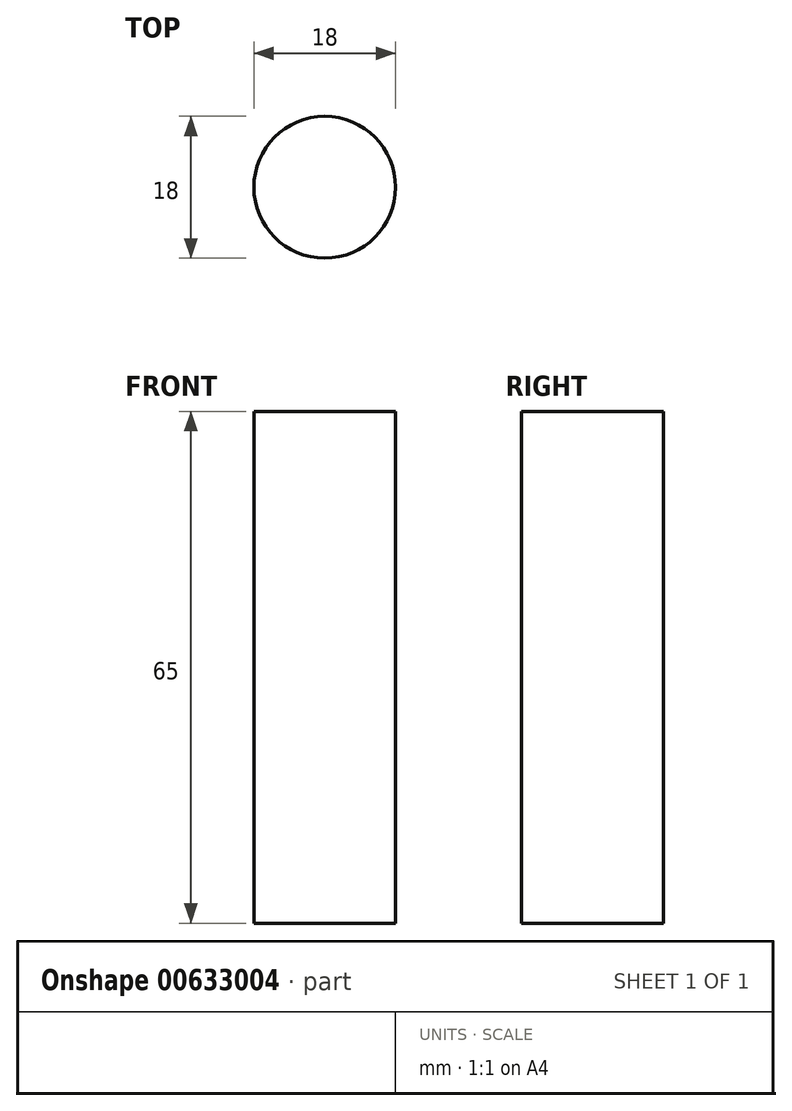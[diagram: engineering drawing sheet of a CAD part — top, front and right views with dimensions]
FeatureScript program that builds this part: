
annotation { "Feature Type Name" : "Feature", "Feature Type Description" : "" }
export const myFeature = defineFeature(function(context is Context, id is Id, definition is map)
    precondition{}
    {
        {
            var Q0;
            Q0=qCreatedBy(makeId("Top.planeOp"),FACE);
            var sketch = newSketch(context, id + "F0", { "sketchPlane" : qUnion([Q0])});
            skCircle(sketch, "E0", {"center": v(0, 0) * mm, "radius": 9 * mm});
            skSolve(sketch);
        }
        {
            var Q0;
            Q0=qSketchRegion(id+"F0",true);
            extrude(context, id + "F1", {"entities" : qUnion([Q0]), "depth" : 65 * mm});
        }
    });
